FCSTD DOCUMENT  (FreeCAD 1.0R39319 (Git))
Label: week 1 sketch  3
License: All rights reserved
LicenseURL: https://en.wikipedia.org/wiki/All_rights_reserved
objects: Sketcher::SketchObject×1, PartDesign::Body×1
note: 3 computed .brp shape members not serialized (recipe doc carries the construction recipe); baked Part::Feature solids carry a one-line shape summary decoded from their .brp

FEATURE [Sketcher::SketchObject] Sketch
  ArcFitTolerance = 1e-06
  AttachmentSupport = -> [XY_Plane]
  FullyConstrained = true
  MakeInternals = false
  MapMode = 5
  sketch-geometry (24):
    g0: ArcOfCircle CenterX=25.2865 CenterY=111.9 CenterZ=0 NormalX=0 NormalY=0 NormalZ=1 AngleXU=0 Radius=22 StartAngle=3e-16 EndAngle=3.14159
    g1: ArcOfCircle CenterX=25.2865 CenterY=83.9 CenterZ=0 NormalX=0 NormalY=0 NormalZ=1 AngleXU=0 Radius=22 StartAngle=3.14159 EndAngle=6.28319
    g2: LineSegment StartX=47.2865 StartY=111.9 StartZ=0 EndX=47.2865 EndY=83.9 EndZ=0
    g3: LineSegment StartX=3.28651 StartY=111.9 StartZ=0 EndX=3.28651 EndY=83.9 EndZ=0
    g4: ArcOfCircle CenterX=25.2865 CenterY=111.9 CenterZ=0 NormalX=0 NormalY=0 NormalZ=1 AngleXU=0 Radius=10 StartAngle=5.70188 EndAngle=9.98847
    g5: LineSegment StartX=16.8336 StartY=106.557 StartZ=0 EndX=16.8336 EndY=92.5569 EndZ=0
    g6: LineSegment StartX=33.644 StartY=106.409 StartZ=0 EndX=33.644 EndY=92.4089 EndZ=0
    g7: LineSegment StartX=13.948 StartY=89.5591 StartZ=0 EndX=13.948 EndY=83.9 EndZ=0
    g8: ArcOfCircle CenterX=25.2865 CenterY=83.9 CenterZ=0 NormalX=0 NormalY=0 NormalZ=1 AngleXU=0 Radius=11.3385 StartAngle=3.14159 EndAngle=6.28319
    g9: LineSegment StartX=36.625 StartY=89.409 StartZ=0 EndX=36.625 EndY=83.9 EndZ=0
    g10: ArcOfCircle CenterX=16.948 CenterY=89.5591 CenterZ=0 NormalX=0 NormalY=0 NormalZ=1 AngleXU=0 Radius=3 StartAngle=1.60893 EndAngle=3.14159
    g11: ArcOfCircle CenterX=33.625 CenterY=89.409 CenterZ=0 NormalX=0 NormalY=0 NormalZ=1 AngleXU=0 Radius=3 StartAngle=1e-16 EndAngle=1.56448
    g12: LineSegment [constr] StartX=25.2865 StartY=138.789 StartZ=0 EndX=25.2865 EndY=-16.881 EndZ=0
    g13: ArcOfCircle CenterX=25.2865 CenterY=31.4798 CenterZ=0 NormalX=0 NormalY=0 NormalZ=1 AngleXU=0 Radius=12 StartAngle=6.2031 EndAngle=9.50486
    g14: ArcOfCircle CenterX=25.2865 CenterY=6.47981 CenterZ=0 NormalX=0 NormalY=0 NormalZ=1 AngleXU=0 Radius=10 StartAngle=3.22168 EndAngle=6.2031
    g15: LineSegment StartX=13.325 StartY=30.5198 StartZ=0 EndX=15.3186 EndY=5.67981 EndZ=0
    g16: LineSegment StartX=37.248 StartY=30.5198 StartZ=0 EndX=35.2545 EndY=5.67981 EndZ=0
    g17: LineSegment StartX=4.68891 StartY=119.629 StartZ=0 EndX=-4.38848 EndY=97.1342 EndZ=0
    g18: ArcOfCircle CenterX=25.2865 CenterY=85.1595 CenterZ=0 NormalX=0 NormalY=0 NormalZ=1 AngleXU=0 Radius=32 StartAngle=2.75805 EndAngle=3.80125
    g19: ArcOfCircle CenterX=-23.7061 CenterY=47.1631 CenterZ=0 NormalX=0 NormalY=0 NormalZ=1 AngleXU=0 Radius=30 StartAngle=5.48764 EndAngle=6.94284
    g20: ArcOfCircle CenterX=25.2865 CenterY=85.1595 CenterZ=0 NormalX=0 NormalY=0 NormalZ=1 AngleXU=0 Radius=32 StartAngle=5.62353 EndAngle=6.66719
    g21: LineSegment StartX=46.0002 StartY=119.312 StartZ=0 EndX=54.9561 EndY=97.1477 EndZ=0
    g22: ArcOfCircle CenterX=74.2791 CenterY=47.1631 CenterZ=0 NormalX=0 NormalY=0 NormalZ=1 AngleXU=0 Radius=30 StartAngle=2.48194 EndAngle=3.93714
    g23: ArcOfCircle CenterX=25.2865 CenterY=-2.83415 CenterZ=0 NormalX=0 NormalY=0 NormalZ=1 AngleXU=0 Radius=40 StartAngle=2.34605 EndAngle=7.07873
  constraints (71):
    c: Tangent(g0,g2) = 1.5708
    c: Tangent(g0,g3) = -1.5708
    c: Tangent(g1,g2) = 1.5708
    c: Tangent(g1,g3) = -1.5708
    c: Equal(g0,g1)
    c: Vertical(g3)
    c: DistanceY(g1,g0) = 28
    c: Coincident(g4,g0)
    c: Radius(g4) = 10
    c: Coincident(g5,g4)
    c: Vertical(g5)
    c: Vertical(g6)
    c: DistanceY(g5,g5) = 14
    c: Vertical(g7)
    c: Tangent(g7,g8) = -1.5708
    c: Coincident(g8,g1)
    c: Coincident(g9,g8)
    c: Vertical(g9)
    c: Horizontal(g7,g8)
    c: Tangent(g7,g10) = -1.5708
    c: Tangent(g9,g11) = 1.5708
    c: Coincident(g11,g6)
    c: Coincident(g10,g5)
    c: Radius(g11) = 3
    c: Equal(g11,g10)
    c: Coincident(g4,g6)
    c: PointOnObject(g0,g12)
    c: PointOnObject(g1,g12)
    c: Radius(g1) = 22
    c: PointOnObject(g13,g12)
    c: PointOnObject(g14,g12)
    c: Equal(g5,g6)
    c: PointOnObject(g17,g0)
    c: Tangent(g17,g18) = -1.5708
    c: PointOnObject(g18,g-2)
    c: Tangent(g18,g19) = 1.5708
    c: Tangent(g21,g20) = 1.5708
    c: Tangent(g20,g22) = 1.5708
    c: DistanceY(g14,g13) = 25
    c: Tangent(g19,g23) = 1.5708
    c: Coincident(g23,g22)
    c: Radius(g23) = 40
    c: Diameter(g13) = 24
    c: Diameter(g14) = 20
    c: Tangent(g13,g16) = 1.5708
    c: Tangent(g13,g15) = -1.5708
    c: Tangent(g14,g15) = -1.5708
    c: Tangent(g14,g16) = 1.5708
    c: Radius(g18) = 32
    c: PointOnObject(g18,g12)
    c: Equal(g18,g20)
    c: Coincident(g20,g18)
    c: Radius(g19) = 30
    c: PointOnObject(g21,g0)
    c: Equal(g19,g22)
    c: Horizontal(g19,g22)
    c: Horizontal(g18,g20)
    c: Block(g6)
    c: Block(g10)
    c: Block(g11)
    c: Block(g19)
    c: Block(g23)
    c: Block(g17)
    c: Block(g21)
    c: Block(g8)
    c: Block(g4)
    c: Block(g12)
    c: Block(g18)
    c: Block(g20)
    c: Block(g22)
    c: Block(g16)
FEATURE [PartDesign::Body] Body
  AllowCompound = false
  Group = -> [Sketch]
  Origin = -> Origin
